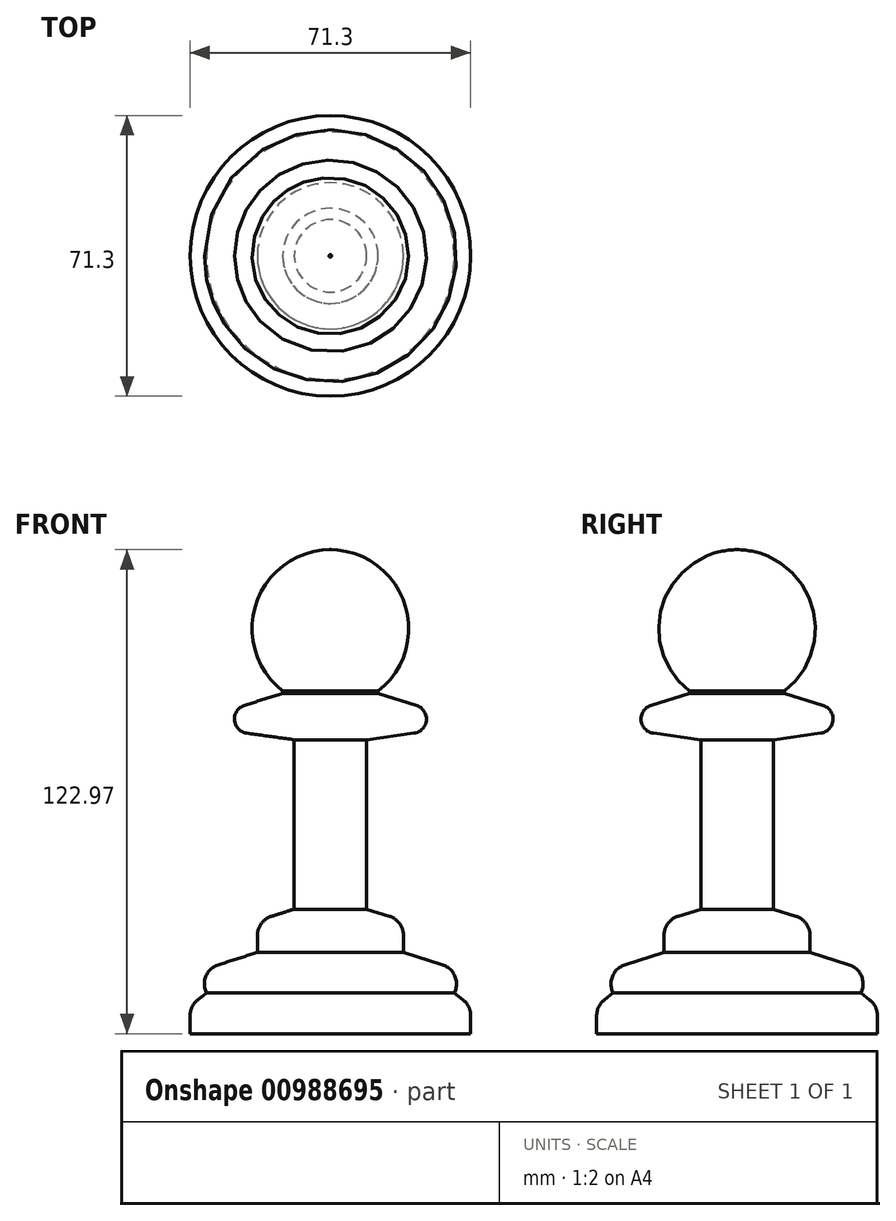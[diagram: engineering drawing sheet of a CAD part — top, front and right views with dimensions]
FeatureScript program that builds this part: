
annotation { "Feature Type Name" : "Feature", "Feature Type Description" : "" }
export const myFeature = defineFeature(function(context is Context, id is Id, definition is map)
    precondition{}
    {
        {
            var Q0;
            Q0=qCreatedBy(makeId("Front.planeOp"),FACE);
            var sketch = newSketch(context, id + "F0", { "sketchPlane" : qUnion([Q0])});
            skLineSegment(sketch, "E0", {"start": v(35.65, -74.69) * mm, "end": v(35.65, -67.6) * mm});
            skLineSegment(sketch, "E1", {"start": v(35.65, -67.6) * mm, "end": v(31.46, -64.36) * mm});
            skLineSegment(sketch, "E2", {"start": v(31.46, -64.36) * mm, "end": v(35.3, -59.36) * mm});
            skLineSegment(sketch, "E3", {"start": v(35.3, -59.36) * mm, "end": v(18.55, -54.04) * mm});
            skLineSegment(sketch, "E4", {"start": v(18.55, -54.04) * mm, "end": v(18.55, -45.98) * mm});
            skLineSegment(sketch, "E5", {"start": v(18.55, -45.98) * mm, "end": v(9.2, -43.07) * mm});
            skLineSegment(sketch, "E6", {"start": v(9.2, -43.07) * mm, "end": v(9.2, 0) * mm});
            skLineSegment(sketch, "E7", {"start": v(9.2, 0) * mm, "end": v(37.29, 3.88) * mm});
            skLineSegment(sketch, "E8", {"start": v(37.29, 3.88) * mm, "end": v(12.1, 11.77) * mm});
            skLineSegment(sketch, "E9", {"start": v(12.1, 11.77) * mm, "end": v(12.1, 12.35) * mm});
            skArc(sketch, "E10", {"start": v(12.1, 12.35) * mm, "mid": v(18.85, 34.63) * mm, "end": v(0, 48.28) * mm});
            skLineSegment(sketch, "E11", {"start": v(35.65, -74.69) * mm, "end": v(0, -74.69) * mm});
            skLineSegment(sketch, "E12", {"start": v(0, -74.69) * mm, "end": v(0, 48.28) * mm});
            skSolve(sketch);
        }
        {
            var Q0;
            Q0=makeQuery(id+"F0.imprint","IMPRINT",FACE,{"disambiguationData":[TD([[makeQuery(id+"F0.imprint","IMPRINT",EDGE,{"derivedFrom":sQuery(id+"F0.wireOp",EDGE,"E0")}),1.0]])]});
            var Q1;
            Q1=sQuery(id+"F0.wireOp",EDGE,"E12");
            revolve(context, id + "F1", {"surfaceOperationType" : NewSurfaceOperationType.NEW, "entities" : qUnion([Q0]), "axis" : qUnion([Q1]), "revolveType" : RevolveType.FULL});
        }
        {
            var Q0;
            Q0=makeQuery(id+"F1.opRevolve","SWEPT_EDGE",EDGE,{"disambiguationData":[OSD([sQuery(id+"F0.wireOp",EDGE,"E7"),sQuery(id+"F0.wireOp",EDGE,"E8")])]});
            fillet(context, id + "F2", {"entities" : qUnion([Q0]), "radius" : 3.63 * mm, "tangentPropagation" : true, "allowEdgeOverflow" : false});
        }
        {
            var Q0;
            Q0=makeQuery(id+"F1.opRevolve","SWEPT_EDGE",EDGE,{"disambiguationData":[OSD([sQuery(id+"F0.wireOp",EDGE,"E2"),sQuery(id+"F0.wireOp",EDGE,"E3")])]});
            fillet(context, id + "F3", {"entities" : qUnion([Q0]), "radius" : 5.08 * mm, "tangentPropagation" : true, "allowEdgeOverflow" : false});
        }
        {
            var Q0;
            Q0=makeQuery(id+"F1.opRevolve","SWEPT_EDGE",EDGE,{"disambiguationData":[OSD([sQuery(id+"F0.wireOp",EDGE,"E0"),sQuery(id+"F0.wireOp",EDGE,"E1")])]});
            fillet(context, id + "F4", {"entities" : qUnion([Q0]), "radius" : 5.08 * mm, "tangentPropagation" : true, "allowEdgeOverflow" : false});
        }
        {
            var Q0;
            {var subQ0=sQuery(id+"F0.wireOp",EDGE,"E4");Q0=makeQuery(id+"FDtBr9bhmlCPKfE_1.opFillet","BLEND_EDGE",EDGE,{"blendedFrom":[makeQuery(id+"F1.opRevolve","SWEPT_EDGE",EDGE,{"disambiguationData":[OSD([sQuery(id+"F0.wireOp",EDGE,"E3"),subQ0])]}),makeQuery(id+"F1.opRevolve","SWEPT_FACE",FACE,{"disambiguationData":[OSD([subQ0])]})],"blendedInto":[makeQuery(id+"F1.opRevolve","SWEPT_FACE",FACE,{"disambiguationData":[OSD([subQ0])]})]});}
            var Q1;
            Q1=makeQuery(id+"F1.opRevolve","SWEPT_EDGE",EDGE,{"disambiguationData":[OSD([sQuery(id+"F0.wireOp",EDGE,"E4"),sQuery(id+"F0.wireOp",EDGE,"E5")])]});
            fillet(context, id + "F5", {"entities" : qUnion([Q0, Q1]), "radius" : 5.08 * mm, "tangentPropagation" : true, "allowEdgeOverflow" : false});
        }
    });
